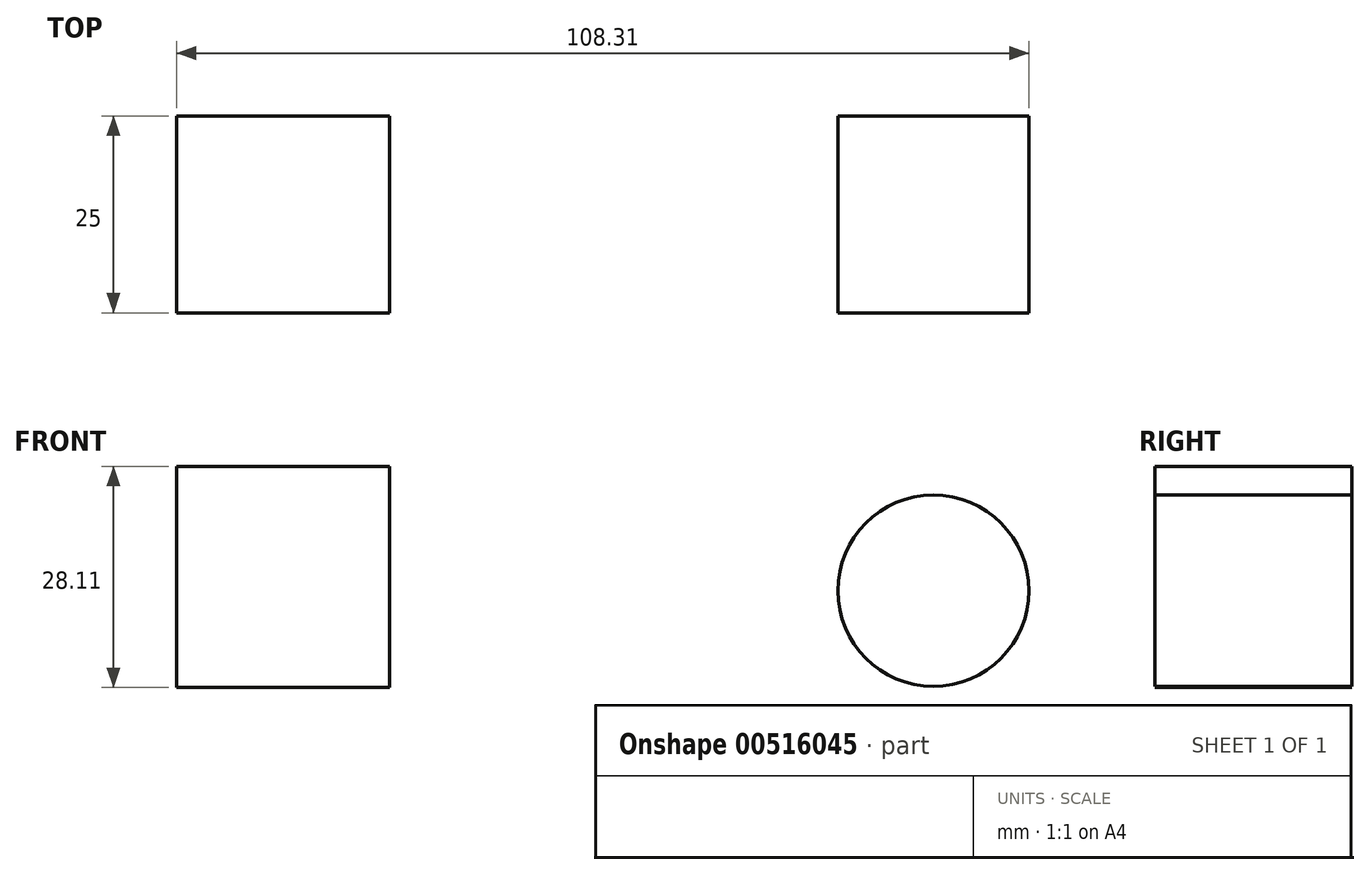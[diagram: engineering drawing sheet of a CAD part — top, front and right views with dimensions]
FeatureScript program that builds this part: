
annotation { "Feature Type Name" : "Feature", "Feature Type Description" : "" }
export const myFeature = defineFeature(function(context is Context, id is Id, definition is map)
    precondition{}
    {
        {
            var Q0;
            Q0=qCreatedBy(makeId("Front.planeOp"),FACE);
            var sketch = newSketch(context, id + "F0", { "sketchPlane" : qUnion([Q0])});
            skLineSegment(sketch, "E0.bottom", {"start": v(-46.2, 53.1) * mm, "end": v(-19.1, 53.1) * mm});
            skLineSegment(sketch, "E0.top", {"start": v(-46.2, 25) * mm, "end": v(-19.1, 25) * mm});
            skLineSegment(sketch, "E0.left", {"start": v(-46.2, 53.1) * mm, "end": v(-46.2, 25) * mm});
            skLineSegment(sketch, "E0.right", {"start": v(-19.1, 53.1) * mm, "end": v(-19.1, 25) * mm});
            skCircle(sketch, "E1", {"center": v(49.97, 37.29) * mm, "radius": 12.14 * mm});
            skSolve(sketch);
        }
        {
            var Q0;
            Q0 = qSketchRegion(id + "F0", true);
            extrude(context, id + "F1", {"entities" : qUnion([Q0]), "depth" : 25 * mm, "offsetDistance" : 25 * mm});
        }
        {
            var Q0;
            Q0 = qSketchRegion(id + "F0", true);
            extrude(context, id + "F2", {"entities" : qUnion([Q0]), "depth" : 25 * mm, "offsetDistance" : 25 * mm});
        }
    });
